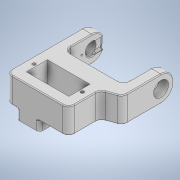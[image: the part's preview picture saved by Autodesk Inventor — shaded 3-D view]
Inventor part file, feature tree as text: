
AUTODESK INVENTOR PART (.ipt)
format: ipt  version: 2020.3 (Build 243373000, 373)  size: 465,408 bytes
history: native  units: mm
features: sketch x8, other x3, plane x3
ambient origin geometry x8: Origin, YZ Plane, XZ Plane, XY Plane, X Axis, Y Axis, Z Axis, Center Point
bodies: Solid1 (feature_tree)
feature tree (14):
  other  "LegStart_v1.ipt"
  plane  "Work Plane4"
  plane  "Work Plane5"
  other  "Solid1::LegStart_v1.ipt"
  other  "TaggingFeature1"
  sketch  "Sketch1"  dims[d0=10.0mm]
  sketch  "Sketch2"  dims[d1=16.0mm]
  sketch  "Sketch3"  dims[d2=-7.5mm]
  sketch  "Sketch8"
  sketch  "Sketch9"
  sketch  "Sketch10"
  sketch  "Sketch11"
  sketch  "Sketch12"
  plane  "Work Plane1"
